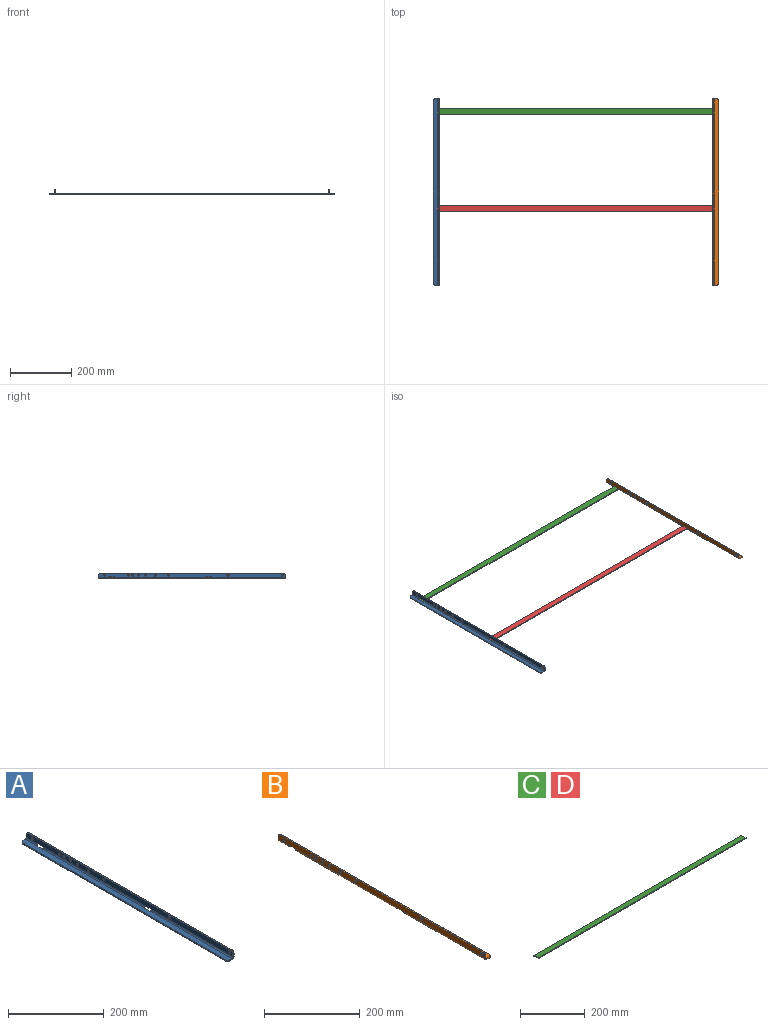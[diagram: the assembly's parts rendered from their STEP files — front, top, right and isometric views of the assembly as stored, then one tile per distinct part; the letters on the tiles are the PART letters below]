
ASSEMBLY  parts=4 mates=3
PART A: 35 faces, bbox 19.1x609.6x19.1 mm
  f0: plane 596.9x3.05mm, normal (0,0,1), area 1819.4mm2, adj f3,f4,f26,f34
  f1: plane 12.7x12.7mm, normal (0,-1,0), area 62.1mm2, adj f4,f22,f23,f26,f27,f29,f31,f34
  f2: plane 12.7x12.7mm, normal (0,1,0), area 62.1mm2, adj f3,f20,f22,f23,f24,f26,f30,f34
  f3: cylinder r=6.35mm len=6.35mm, axis (-1,0,0), area 30.4mm2, adj f0,f2,f26,f34
  f4: cylinder r=6.35mm len=6.35mm, axis (1,0,0), area 30.4mm2, adj f0,f1,f26,f34
  f5: cylinder r=3.49mm len=6.99mm, axis (1,0,0), area 66.9mm2, adj f26,f34
  f6: cylinder r=3.49mm len=6.99mm, axis (1,0,0), area 66.9mm2, adj f26,f34
  f7: cylinder r=3.49mm len=6.99mm, axis (1,0,0), area 66.9mm2, adj f26,f34
  f8: plane 6.35x6.35mm, normal (0,-1,0), area 23.4mm2, adj f10,f21,f22,f23,f25,f26,f32,f34
  f9: plane 6.35x6.35mm, normal (0,1,0), area 23.4mm2, adj f10,f22,f23,f26,f27,f29,f32,f34
  f10: plane 19.3x3.05mm, normal (0,0,-1), area 58.8mm2, adj f8,f9,f26,f34
  f11: plane 6.35x6.35mm, normal (0,-1,0), area 23.4mm2, adj f13,f20,f22,f23,f24,f26,f33,f34
  f12: plane 6.35x6.35mm, normal (0,1,0), area 23.4mm2, adj f13,f21,f22,f23,f25,f26,f33,f34
  f13: plane 19.3x3.05mm, normal (0,0,-1), area 58.8mm2, adj f11,f12,f26,f34
  f14: cylinder r=3.3mm len=6.6mm, axis (1,0,0), area 63.2mm2, adj f26,f34
  f15: cylinder r=3.3mm len=6.6mm, axis (1,0,0), area 63.2mm2, adj f26,f34
  f16: cylinder r=3.3mm len=6.6mm, axis (1,0,0), area 63.2mm2, adj f26,f34
  f17: cylinder r=3.3mm len=6.6mm, axis (1,0,0), area 63.2mm2, adj f26,f34
  f18: cylinder r=3.3mm len=6.6mm, axis (1,0,0), area 63.2mm2, adj f26,f34
  f19: cylinder r=3.3mm len=6.6mm, axis (1,0,0), area 63.2mm2, adj f26,f34
  f20: cylinder r=3.05mm len=31.5mm, axis (0,1,0), area 150.8mm2, adj f2,f11,f22,f26
  f21: cylinder r=3.05mm len=298.2mm, axis (0,1,0), area 1427.7mm2, adj f8,f12,f22,f26
  f22: plane 609.6x12.95mm, normal (0,0,1), area 7869.6mm2, adj f1,f2,f8,f9,f11,f12,f20,f21
  f23: plane 609.6x12.95mm, normal (0,0,-1), area 7869.6mm2, adj f1,f2,f8,f9,f11,f12,f24,f25
  f24: cylinder r=6.1mm len=31.5mm, axis (0,1,0), area 301.6mm2, adj f2,f11,f23,f34
  f25: cylinder r=6.1mm len=298.2mm, axis (0,1,0), area 2855.4mm2, adj f8,f12,f23,f34
  f26: plane 609.6x12.95mm, normal (-1,0,0), area 7549.2mm2, adj f0,f1,f2,f3,f4,f5,f6,f7
  f27: cylinder r=3.05mm len=241.3mm, axis (0,1,0), area 1155.3mm2, adj f1,f9,f22,f26
  f28: plane 596.9x3.05mm, normal (-1,0,0), area 1819.4mm2, adj f22,f23,f30,f31
  f29: cylinder r=6.1mm len=241.3mm, axis (0,1,0), area 2310.6mm2, adj f1,f9,f23,f34
  f30: cylinder r=6.35mm len=6.35mm, axis (0,0,-1), area 30.4mm2, adj f2,f22,f23,f28
  f31: cylinder r=6.35mm len=6.35mm, axis (0,0,1), area 30.4mm2, adj f1,f22,f23,f28
  f32: plane 19.3x3.05mm, normal (1,0,0), area 58.8mm2, adj f8,f9,f22,f23
  f33: plane 19.3x3.05mm, normal (1,0,0), area 58.8mm2, adj f11,f12,f22,f23
  f34: plane 609.6x12.95mm, normal (1,0,0), area 7549.2mm2, adj f0,f1,f2,f3,f4,f5,f6,f7
PART B: 35 faces, bbox 19.1x609.6x19.1 mm
  f0: plane 596.9x3.05mm, normal (1,0,0), area 1819.4mm2, adj f1,f2,f7,f9
  f1: cylinder r=6.35mm len=6.35mm, axis (0,0,1), area 30.4mm2, adj f0,f7,f9,f22
  f2: cylinder r=6.35mm len=6.35mm, axis (0,0,-1), area 30.4mm2, adj f0,f7,f9,f21
  f3: plane 19.3x3.05mm, normal (-1,0,0), area 58.8mm2, adj f7,f9,f14,f20
  f4: cylinder r=3.05mm len=241.3mm, axis (0,1,0), area 1155.3mm2, adj f7,f14,f22,f32
  f5: cylinder r=3.05mm len=31.5mm, axis (0,1,0), area 150.8mm2, adj f7,f19,f21,f32
  f6: plane 19.3x3.05mm, normal (-1,0,0), area 58.8mm2, adj f7,f9,f17,f19
  f7: plane 609.6x12.95mm, normal (0,0,1), area 7869.6mm2, adj f0,f1,f2,f3,f4,f5,f6,f8
  f8: cylinder r=3.05mm len=298.2mm, axis (0,1,0), area 1427.7mm2, adj f7,f17,f20,f32
  f9: plane 609.6x12.95mm, normal (0,0,-1), area 7869.6mm2, adj f0,f1,f2,f3,f6,f13,f14,f16
  f10: cylinder r=6.35mm len=6.35mm, axis (1,0,0), area 30.4mm2, adj f22,f23,f32,f34
  f11: cylinder r=6.35mm len=6.35mm, axis (-1,0,0), area 30.4mm2, adj f21,f23,f32,f34
  f12: plane 19.3x3.05mm, normal (0,0,-1), area 58.8mm2, adj f14,f20,f32,f34
  f13: cylinder r=6.1mm len=241.3mm, axis (0,1,0), area 2310.6mm2, adj f9,f14,f22,f34
  f14: plane 6.35x6.35mm, normal (0,1,0), area 23.4mm2, adj f3,f4,f7,f9,f12,f13,f32,f34
  f15: plane 19.3x3.05mm, normal (0,0,-1), area 58.8mm2, adj f17,f19,f32,f34
  f16: cylinder r=6.1mm len=298.2mm, axis (0,1,0), area 2855.4mm2, adj f9,f17,f20,f34
  f17: plane 6.35x6.35mm, normal (0,1,0), area 23.4mm2, adj f6,f7,f8,f9,f15,f16,f32,f34
  f18: cylinder r=6.1mm len=31.5mm, axis (0,1,0), area 301.6mm2, adj f9,f19,f21,f34
  f19: plane 6.35x6.35mm, normal (0,-1,0), area 23.4mm2, adj f5,f6,f7,f9,f15,f18,f32,f34
  f20: plane 6.35x6.35mm, normal (0,-1,0), area 23.4mm2, adj f3,f7,f8,f9,f12,f16,f32,f34
  f21: plane 12.7x12.7mm, normal (0,1,0), area 62.1mm2, adj f2,f5,f7,f9,f11,f18,f32,f34
  f22: plane 12.7x12.7mm, normal (0,-1,0), area 62.1mm2, adj f1,f4,f7,f9,f10,f13,f32,f34
  f23: plane 596.9x3.05mm, normal (0,0,1), area 1819.4mm2, adj f10,f11,f32,f34
  f24: cylinder r=3.49mm len=6.99mm, axis (1,0,0), area 66.9mm2, adj f32,f34
  f25: cylinder r=3.49mm len=6.99mm, axis (1,0,0), area 66.9mm2, adj f32,f34
  f26: cylinder r=3.49mm len=6.99mm, axis (1,0,0), area 66.9mm2, adj f32,f34
  f27: cylinder r=3.3mm len=6.6mm, axis (1,0,0), area 63.2mm2, adj f32,f34
  f28: cylinder r=3.3mm len=6.6mm, axis (1,0,0), area 63.2mm2, adj f32,f34
  f29: cylinder r=3.3mm len=6.6mm, axis (1,0,0), area 63.2mm2, adj f32,f34
  f30: cylinder r=3.3mm len=6.6mm, axis (1,0,0), area 63.2mm2, adj f32,f34
  f31: cylinder r=3.3mm len=6.6mm, axis (1,0,0), area 63.2mm2, adj f32,f34
  f32: plane 609.6x12.95mm, normal (1,0,0), area 7549.2mm2, adj f4,f5,f8,f10,f11,f12,f14,f15
  f33: cylinder r=3.3mm len=6.6mm, axis (1,0,0), area 63.2mm2, adj f32,f34
  f34: plane 609.6x12.95mm, normal (-1,0,0), area 7549.2mm2, adj f10,f11,f12,f13,f14,f15,f16,f17
PART C: 6 faces, bbox 906.6x19.1x3 mm
  f0: plane 906.63x3.05mm, normal (0,-1,0), area 2763.4mm2, adj f1,f3,f4,f5
  f1: plane 906.63x19.05mm, normal (0,0,-1), area 17271.3mm2, adj f0,f2,f4,f5
  f2: plane 906.63x3.05mm, normal (0,1,0), area 2763.4mm2, adj f1,f3,f4,f5
  f3: plane 906.63x19.05mm, normal (0,0,1), area 17271.3mm2, adj f0,f2,f4,f5
  f4: plane 19.05x3.05mm, normal (1,0,0), area 58.1mm2, adj f0,f1,f2,f3
  f5: plane 19.05x3.05mm, normal (-1,0,0), area 58.1mm2, adj f0,f1,f2,f3
PART D: same geometry as C
PLACE A t=(-446.96,358.78,0)mm
PLACE B t=(446.96,358.78,0)mm
PLACE C t=(0,317.5,0)mm
PLACE D at identity fixed
MATE fastened C.f3 <-> A.f22  axis (0,0,1) through (-453.31,307.98,3.05)mm
MATE fastened B.f7 <-> D.f3  axis (0,0,1) through (453.31,-9.53,3.05)mm
MATE fastened D.f3 <-> A.f22  axis (0,0,1) through (-453.31,-9.52,3.05)mm
